# Revit family: Zumtobel MICROS2
name_source: partatom
category: Lighting Fixtures
revit_build: Autodesk Revit 2016 (Build: 20150220_1215(x64)
units: mm (PartAtom-declared; Revit-internal decimal feet)

## family parameters
Cut with Voids When Loaded = No
Host = Face
Light Source = Yes
OmniClass Number = 23.80.70.11
OmniClass Title = Luminaries for Internal Lighting
Part Type = Normal
Room Calculation Point = No
Round Connector Dimension = Use Diameter
Shared = No

## types (2) — shared parameters
Assembly Code = D5020200
Color Filter = 16777215
Description = LED ceiling-recessed luminaire
Dimming Lamp Color Temperature Shift = <None>
Lamp = LED
Manufacturer = Zumtobel Lighting
Tilt Angle = 0.00°
URL = http://www.zumtobel.com
Voltage = 230 V
zero-valued in all types: Default Elevation

## per-type parameters (varying)
| type | Apparent Load | Height | Length | Model | Opening Radius | Photometric Web File | R100 | R68 | Width |
| MICROS2 R100 | 14 VA | 74 mm  [stored 0.242782 ft] | 112 mm  [stored 0.367454 ft] | 60300020 | 50 mm  [stored 0.164042 ft] | 60300020_(STD_LEO).IES | Yes | No | 112 mm  [stored 0.367454 ft] |
| MICROS2 R65 | 11 VA | 49 mm  [stored 0.160761 ft] | 80 mm  [stored 0.262467 ft] | 60300017 | 32 mm  [stored 0.104987 ft] | 60300017_(STD_LEO).IES | No | Yes | 80 mm  [stored 0.262467 ft] |

note: [stored X ft] marks values corroborated as IEEE doubles in the binary element streams (Revit-internal decimal feet)

## geometry (parser evidence)
native form markers: Sweep x3
no freeform markers — native parametric forms only
